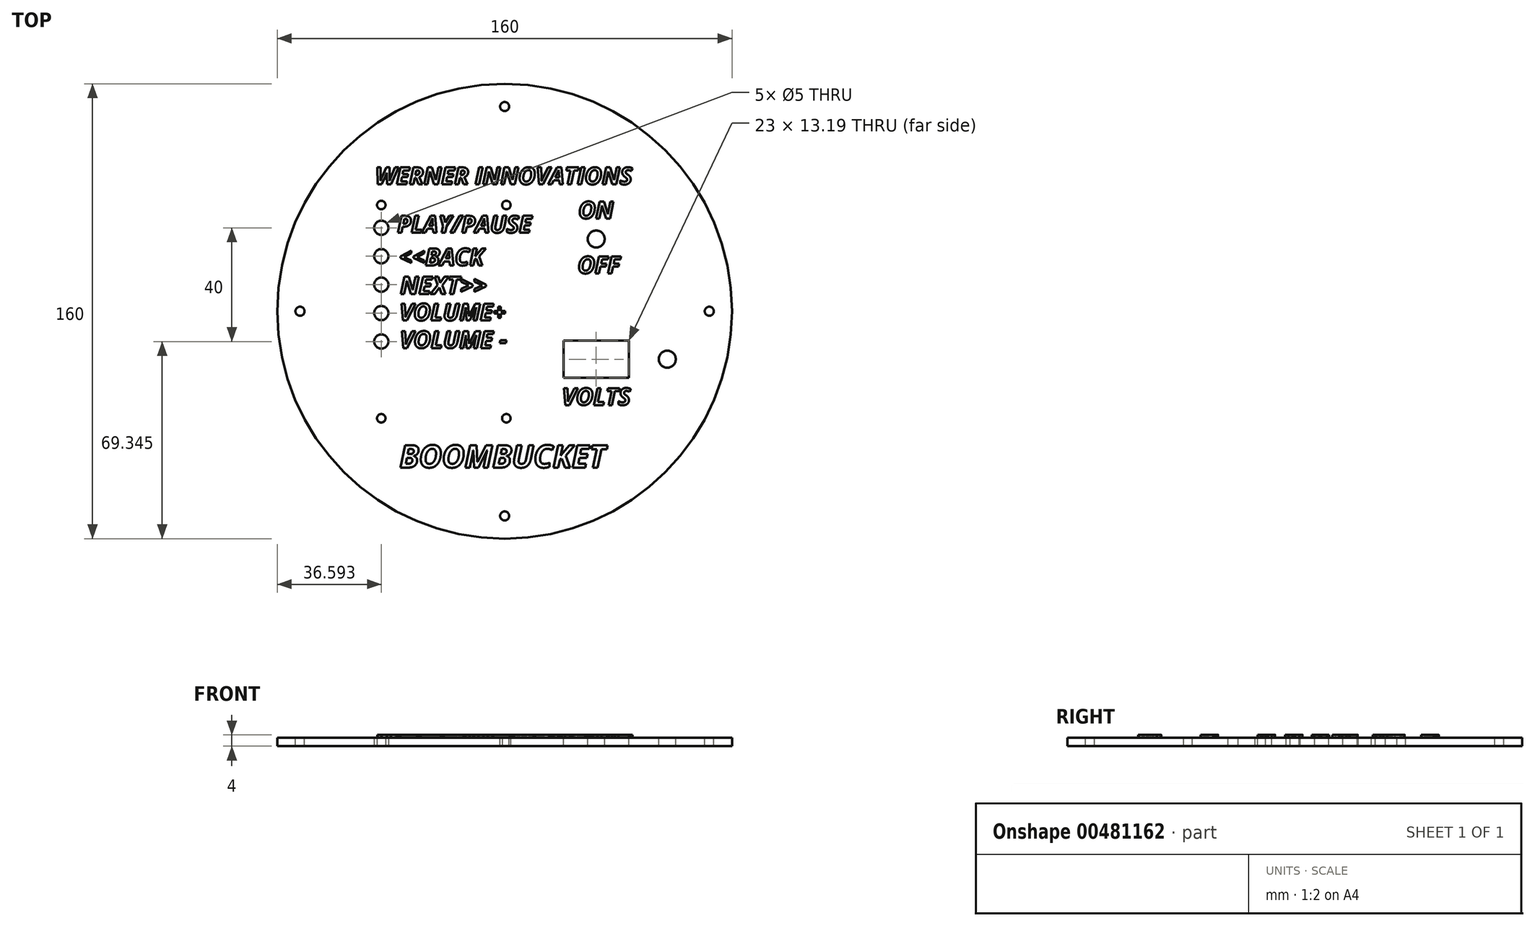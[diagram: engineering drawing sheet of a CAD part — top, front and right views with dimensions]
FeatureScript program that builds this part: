
annotation { "Feature Type Name" : "Feature", "Feature Type Description" : "" }
export const myFeature = defineFeature(function(context is Context, id is Id, definition is map)
    precondition{}
    {
        {
            var Q0;
            Q0=qCreatedBy(makeId("Top.planeOp"),FACE);
            var sketch = newSketch(context, id + "F0", { "sketchPlane" : qUnion([Q0])});
            skCircle(sketch, "E0", {"center": v(0, 0) * mm, "radius": 80 * mm});
            skLineSegment(sketch, "E1.bottom", {"start": v(0.6, -37.66) * mm, "end": v(0.6, 37.34) * mm, "construction": true});
            skLineSegment(sketch, "E1.top", {"start": v(-43.4, -37.66) * mm, "end": v(-43.4, 37.34) * mm, "construction": true});
            skLineSegment(sketch, "E1.left", {"start": v(0.6, -37.66) * mm, "end": v(-43.4, -37.66) * mm, "construction": true});
            skLineSegment(sketch, "E1.right", {"start": v(0.6, 37.34) * mm, "end": v(-43.4, 37.34) * mm, "construction": true});
            skPoint(sketch, "E1.middle", {"position": v(-21.4, -0.16) * mm});
            skCircle(sketch, "E2", {"center": v(0.6, 37.34) * mm, "radius": 1.5 * mm});
            skCircle(sketch, "E3", {"center": v(0.6, -37.66) * mm, "radius": 1.5 * mm});
            skCircle(sketch, "E4", {"center": v(-43.4, -37.66) * mm, "radius": 1.5 * mm});
            skCircle(sketch, "E5", {"center": v(-43.4, 37.34) * mm, "radius": 1.5 * mm});
            skCircle(sketch, "E6", {"center": v(-43.4, 29.34) * mm, "radius": 2.5 * mm});
            skCircle(sketch, "E7", {"center": v(-43.4, 19.34) * mm, "radius": 2.5 * mm});
            skCircle(sketch, "E8", {"center": v(-43.4, 9.34) * mm, "radius": 2.5 * mm});
            skCircle(sketch, "E9", {"center": v(-43.4, -0.66) * mm, "radius": 2.5 * mm});
            skCircle(sketch, "E10", {"center": v(-43.4, -10.66) * mm, "radius": 2.5 * mm});
            skPoint(sketch, "E11.middle", {"position": v(31.72, -0.16) * mm});
            skPoint(sketch, "E11.bottom.end.orphan", {"position": v(38.22, 9.34) * mm});
            skPoint(sketch, "E11.left.start.orphan", {"position": v(38.22, -9.66) * mm});
            skPoint(sketch, "E11.top.end.orphan", {"position": v(25.22, 9.34) * mm});
            skPoint(sketch, "E11.top.start.orphan", {"position": v(25.22, -9.66) * mm});
            skSolve(sketch);
        }
        {
            var Q0;
            Q0 = qSketchRegion(id + "F0", true);
            extrude(context, id + "F1", {"entities" : qUnion([Q0]), "depth" : 3 * mm, "offsetDistance" : 25 * mm});
        }
        {
            var Q0;
            Q0=makeQuery(id+"F1.opExtrude","CAP_FACE",FACE,{"disambiguationData":[OSD([sQuery(id+"F0.wireOp",EDGE,"E0"),sQuery(id+"F0.wireOp",EDGE,"E2"),sQuery(id+"F0.wireOp",EDGE,"E3"),sQuery(id+"F0.wireOp",EDGE,"E4"),sQuery(id+"F0.wireOp",EDGE,"E5"),sQuery(id+"F0.wireOp",EDGE,"E6"),sQuery(id+"F0.wireOp",EDGE,"E7"),sQuery(id+"F0.wireOp",EDGE,"E8"),sQuery(id+"F0.wireOp",EDGE,"E9"),sQuery(id+"F0.wireOp",EDGE,"E10")])],"isStart":false});
            var sketch = newSketch(context, id + "F2", { "sketchPlane" : qUnion([Q0])});
            skLineSegment(sketch, "E12", {"start": v(32.2, 46.26) * mm, "end": v(32.2, -56) * mm, "construction": true});
            skCircle(sketch, "E13", {"center": v(32.2, 25.38) * mm, "radius": 3 * mm});
            skLineSegment(sketch, "E14.bottom", {"start": v(43.7, -10.28) * mm, "end": v(20.7, -10.28) * mm});
            skLineSegment(sketch, "E14.top", {"start": v(43.7, -23.47) * mm, "end": v(20.7, -23.47) * mm});
            skLineSegment(sketch, "E14.left", {"start": v(43.7, -10.28) * mm, "end": v(43.7, -23.47) * mm});
            skLineSegment(sketch, "E14.right", {"start": v(20.7, -10.28) * mm, "end": v(20.7, -23.47) * mm});
            skPoint(sketch, "E14.middle", {"position": v(32.2, -16.88) * mm});
            skCircle(sketch, "E15", {"center": v(57.22, -16.88) * mm, "radius": 3 * mm});
            skSolve(sketch);
        }
        {
            var Q0;
            Q0=makeQuery(id+"F2.imprint","IMPRINT",FACE,{"disambiguationData":[TD([[makeQuery(id+"F2.imprint","IMPRINT",EDGE,{"derivedFrom":sQuery(id+"F2.wireOp",EDGE,"E13")}),-1.0]])]});
            var sketch = newSketch(context, id + "F3", { "sketchPlane" : qUnion([Q0])});
            skText(sketch, "E16", { "text": "PLAY/PAUSE", "fontName": "OpenSans-BoldItalic.ttf"});
            skText(sketch, "E17", { "text": "<<BACK", "fontName": "OpenSans-BoldItalic.ttf"});
            skText(sketch, "E18", { "text": "NEXT>>", "fontName": "OpenSans-BoldItalic.ttf"});
            skText(sketch, "E19", { "text": "VOLUME+", "fontName": "OpenSans-BoldItalic.ttf"});
            skText(sketch, "E20", { "text": "VOLUME -", "fontName": "OpenSans-BoldItalic.ttf"});
            const initialGuessF3  = {"E16": [-0.0378, 0.0276, 1, 0, 0.006], "E17": [-0.03716, 0.0161, 1, 0, 0.00601], "E18": [-0.03675, 0.00601, 1, 0, 0.0062], "E19": [-0.03705, -0.00328, 1, 0, 0.006], "E20": [-0.03696, -0.01298, 1, 0, 0.006]};
            skSetInitialGuess(sketch, initialGuessF3);
            skSolve(sketch);
        }
        {
            var Q0;
            Q0 = qSketchRegion(id + "F2", true);
            extrude(context, id + "F4", {"entities" : qUnion([Q0]), "operationType" : NewBodyOperationType.REMOVE, "oppositeDirection" : true, "depth" : 3 * mm, "offsetDistance" : 25 * mm});
        }
        {
            var Q0;
            Q0 = qSketchRegion(id + "F3", true);
            extrude(context, id + "F5", {"entities" : qUnion([Q0]), "operationType" : NewBodyOperationType.ADD, "depth" : 1 * mm, "offsetDistance" : 25 * mm});
        }
        {
            var Q0;
            {var subQ0=sQuery(id+"F0.wireOp",EDGE,"E10");var subQ1=sQuery(id+"F0.wireOp",EDGE,"E9");var subQ2=sQuery(id+"F0.wireOp",EDGE,"E8");var subQ3=sQuery(id+"F0.wireOp",EDGE,"E7");var subQ4=sQuery(id+"F0.wireOp",EDGE,"E6");var subQ5=sQuery(id+"F0.wireOp",EDGE,"E5");var subQ6=sQuery(id+"F0.wireOp",EDGE,"E0");var subQ7=sQuery(id+"F0.wireOp",EDGE,"E2");var subQ8=sQuery(id+"F0.wireOp",EDGE,"E4");var subQ9=sQuery(id+"F0.wireOp",EDGE,"E3");Q0=makeQuery(id+"F5.boolean.opBoolean","SPLIT",FACE,{"disambiguationData":[TD([makeQuery(id+"F1.opExtrude","SWEPT_FACE",FACE,{"disambiguationData":[OSD([subQ6])]})])],"derivedFrom":makeQuery(id+"F1.opExtrude","CAP_FACE",FACE,{"disambiguationData":[OSD([subQ6,subQ7,subQ9,subQ8,subQ5,subQ4,subQ3,subQ2,subQ1,subQ0])],"isStart":false})});}
            var sketch = newSketch(context, id + "F6", { "sketchPlane" : qUnion([Q0])});
            skText(sketch, "E21", { "text": "ON\n", "fontName": "OpenSans-BoldItalic.ttf"});
            skText(sketch, "E22", { "text": "OFF", "fontName": "OpenSans-BoldItalic.ttf"});
            skText(sketch, "E23", { "text": "VOLTS", "fontName": "OpenSans-BoldItalic.ttf"});
            const initialGuessF6  = {"E21": [0.02591, 0.03261, 1, 0, 0.006], "E22": [0.02568, 0.0133, 1, 0, 0.006], "E23": [0.02015, -0.03301, 1, 0, 0.006]};
            skSetInitialGuess(sketch, initialGuessF6);
            skSolve(sketch);
        }
        {
            var Q0;
            Q0 = qSketchRegion(id + "F6", true);
            extrude(context, id + "F7", {"entities" : qUnion([Q0]), "operationType" : NewBodyOperationType.ADD, "depth" : 1 * mm, "offsetDistance" : 25 * mm});
        }
        {
            var Q0;
            {var subQ231=sQuery(id+"F0.wireOp",EDGE,"E3");var subQ253=sQuery(id+"F0.wireOp",EDGE,"E4");var subQ266=sQuery(id+"F0.wireOp",EDGE,"E2");var subQ285=sQuery(id+"F0.wireOp",EDGE,"E0");var subQ286=makeQuery(id+"F1.opExtrude","SWEPT_FACE",FACE,{"disambiguationData":[OSD([subQ285])]});var subQ314=sQuery(id+"F0.wireOp",EDGE,"E5");var subQ319=sQuery(id+"F0.wireOp",EDGE,"E7");var subQ321=sQuery(id+"F0.wireOp",EDGE,"E6");var subQ326=sQuery(id+"F0.wireOp",EDGE,"E8");var subQ332=sQuery(id+"F0.wireOp",EDGE,"E9");var subQ337=sQuery(id+"F0.wireOp",EDGE,"E10");Q0=makeQuery(id+"F7.boolean.opBoolean","SPLIT",FACE,{"disambiguationData":[TD([subQ286])],"derivedFrom":makeQuery(id+"F5.boolean.opBoolean","SPLIT",FACE,{"disambiguationData":[TD([subQ286])],"derivedFrom":makeQuery(id+"F1.opExtrude","CAP_FACE",FACE,{"disambiguationData":[OSD([subQ285,subQ266,subQ231,subQ253,subQ314,subQ321,subQ319,subQ326,subQ332,subQ337])],"isStart":false})})});}
            var sketch = newSketch(context, id + "F8", { "sketchPlane" : qUnion([Q0])});
            skText(sketch, "E24", { "text": "BOOMBUCKET", "fontName": "OpenSans-BoldItalic.ttf"});
            skText(sketch, "E25", { "text": "WERNER INNOVATIONS", "fontName": "OpenSans-BoldItalic.ttf"});
            const initialGuessF8  = {"E24": [-0.03702, -0.055, 1, 0, 0.00795], "E25": [-0.04556, 0.04463, 1, 0, 0.006]};
            skSetInitialGuess(sketch, initialGuessF8);
            skSolve(sketch);
        }
        {
            var Q0;
            Q0 = qSketchRegion(id + "F8", true);
            extrude(context, id + "F9", {"entities" : qUnion([Q0]), "operationType" : NewBodyOperationType.ADD, "depth" : 1 * mm, "offsetDistance" : 25 * mm});
        }
        {
            var Q0;
            {var subQ29=sQuery(id+"F0.wireOp",EDGE,"E2");var subQ95=sQuery(id+"F0.wireOp",EDGE,"E10");var subQ99=sQuery(id+"F0.wireOp",EDGE,"E9");var subQ103=sQuery(id+"F0.wireOp",EDGE,"E8");var subQ107=sQuery(id+"F0.wireOp",EDGE,"E7");var subQ111=sQuery(id+"F0.wireOp",EDGE,"E6");var subQ115=sQuery(id+"F0.wireOp",EDGE,"E5");var subQ192=sQuery(id+"F0.wireOp",EDGE,"E0");var subQ193=makeQuery(id+"F1.opExtrude","SWEPT_FACE",FACE,{"disambiguationData":[OSD([subQ192])]});var subQ251=sQuery(id+"F0.wireOp",EDGE,"E4");var subQ279=sQuery(id+"F0.wireOp",EDGE,"E3");Q0=makeQuery(id+"F9.boolean.opBoolean","SPLIT",FACE,{"disambiguationData":[TD([subQ193])],"derivedFrom":makeQuery(id+"F7.boolean.opBoolean","SPLIT",FACE,{"disambiguationData":[TD([subQ193])],"derivedFrom":makeQuery(id+"F5.boolean.opBoolean","SPLIT",FACE,{"disambiguationData":[TD([subQ193])],"derivedFrom":makeQuery(id+"F1.opExtrude","CAP_FACE",FACE,{"disambiguationData":[OSD([subQ192,subQ29,subQ279,subQ251,subQ115,subQ111,subQ107,subQ103,subQ99,subQ95])],"isStart":false})})})});}
            var sketch = newSketch(context, id + "F10", { "sketchPlane" : qUnion([Q0])});
            skCircle(sketch, "E26", {"center": v(0, 72) * mm, "radius": 1.6 * mm});
            skCircle(sketch, "E27.MirrorC", {"center": v(0, -72) * mm, "radius": 1.6 * mm});
            skCircle(sketch, "E28", {"center": v(72, 0) * mm, "radius": 1.6 * mm});
            skCircle(sketch, "E29.MirrorC", {"center": v(-72, 0) * mm, "radius": 1.6 * mm});
            skSolve(sketch);
        }
        {
            var Q0;
            Q0 = qSketchRegion(id + "F10", true);
            extrude(context, id + "F11", {"entities" : qUnion([Q0]), "operationType" : NewBodyOperationType.REMOVE, "oppositeDirection" : true, "depth" : 3 * mm, "offsetDistance" : 25 * mm});
        }
    });
